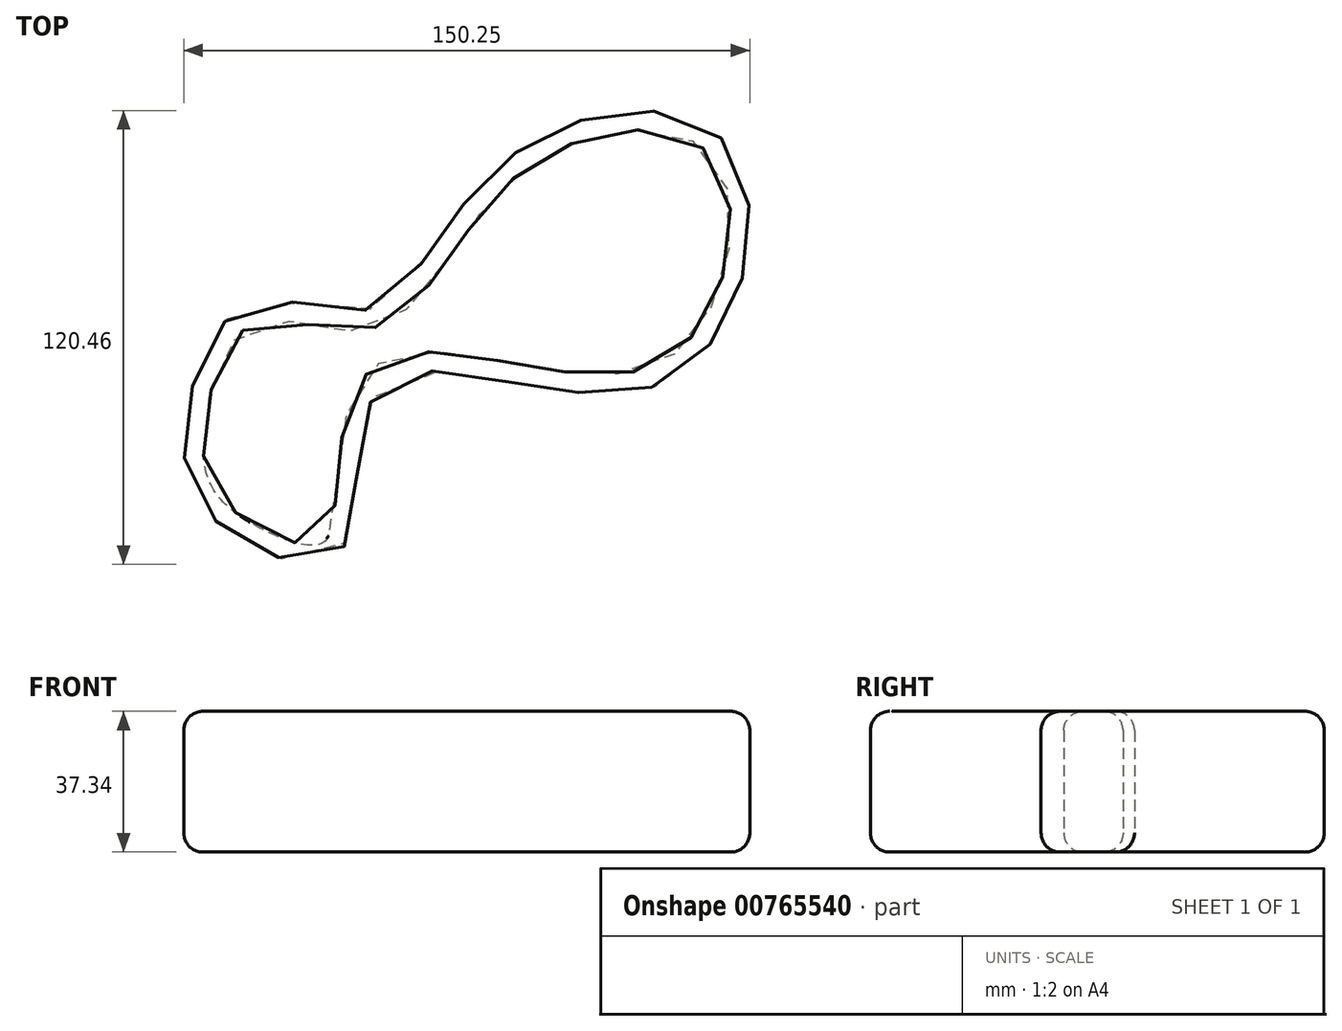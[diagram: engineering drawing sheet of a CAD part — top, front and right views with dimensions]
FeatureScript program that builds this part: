
annotation { "Feature Type Name" : "Feature", "Feature Type Description" : "" }
export const myFeature = defineFeature(function(context is Context, id is Id, definition is map)
    precondition{}
    {
        {
            var Q0;
            Q0=qCreatedBy(makeId("Top.planeOp"),FACE);
            var sketch = newSketch(context, id + "F0", { "sketchPlane" : qUnion([Q0])});
            skFitSpline(sketch, "E0", {"points": [v(-127.33, -19.97) * mm, v(-110.74, 20.63) * mm, v(-78.05, 19.49) * mm, v(-40.88, 59.97) * mm, v(17.22, 62.48) * mm, v(0, 0) * mm, v(-74.06, 0) * mm, v(-85.83, -45.05) * mm, v(-111.64, -41.94) * mm, v(-127.33, -19.97) * mm]});
            skSolve(sketch);
        }
        {
            var Q0;
            Q0 = qSketchRegion(id + "F0", true);
            extrude(context, id + "F1", {"entities" : qUnion([Q0]), "depth" : 37.34 * mm, "offsetDistance" : 25.4 * mm});
        }
        {
            var Q0;
            Q0=makeQuery(id+"F1.opExtrude","CAP_EDGE",EDGE,{"disambiguationData":[OSD([sQuery(id+"F0.wireOp",EDGE,"E0")])],"isStart":true});
            var Q1;
            Q1=makeQuery(id+"F1.opExtrude","CAP_EDGE",EDGE,{"disambiguationData":[OSD([sQuery(id+"F0.wireOp",EDGE,"E0")])],"isStart":false});
            fillet(context, id + "F2", {"entities" : qUnion([Q0, Q1]), "radius" : 5.08 * mm, "tangentPropagation" : true, "allowEdgeOverflow" : false});
        }
    });
